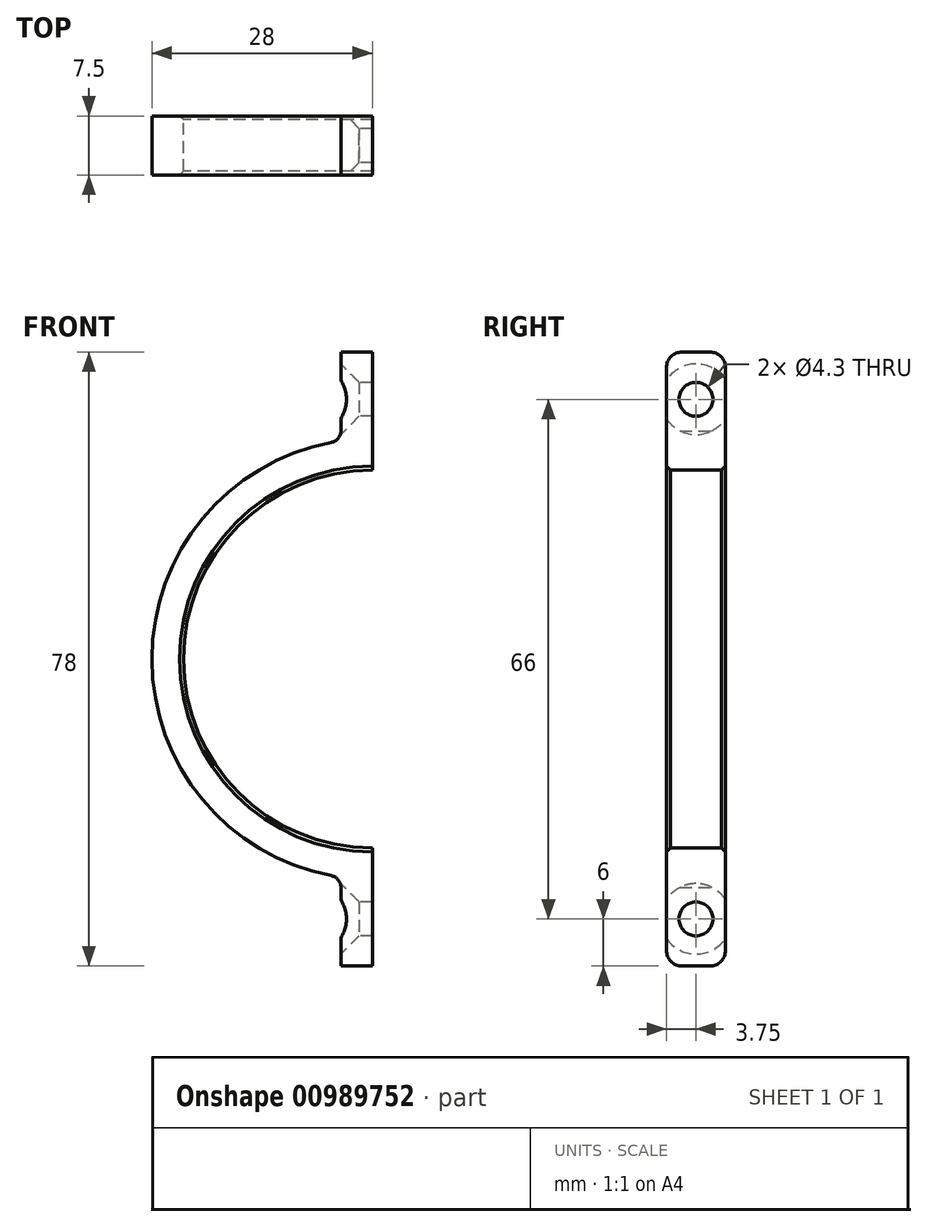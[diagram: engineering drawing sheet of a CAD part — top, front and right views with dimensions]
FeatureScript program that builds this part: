
annotation { "Feature Type Name" : "Feature", "Feature Type Description" : "" }
export const myFeature = defineFeature(function(context is Context, id is Id, definition is map)
    precondition{}
    {
        {
            var Q0;
            Q0=qCreatedBy(makeId("Front.planeOp"),FACE);
            var sketch = newSketch(context, id + "F0", { "sketchPlane" : qUnion([Q0])});
            skArc(sketch, "E0", {"start": v(-5.22, 27.5) * mm, "mid": v(-28, 0) * mm, "end": v(-5.22, -27.5) * mm});
            skArc(sketch, "E1", {"start": v(0, 24) * mm, "mid": v(-24, 0) * mm, "end": v(0, -24) * mm});
            skLineSegment(sketch, "E2", {"start": v(0, 28) * mm, "end": v(0, 24) * mm});
            skLineSegment(sketch, "E3", {"start": v(0, -24) * mm, "end": v(0, -28) * mm});
            skLineSegment(sketch, "E4", {"start": v(-4, 28.98) * mm, "end": v(-4, 39) * mm});
            skLineSegment(sketch, "E5", {"start": v(-4, 39) * mm, "end": v(0, 39) * mm});
            skLineSegment(sketch, "E6", {"start": v(0, 39) * mm, "end": v(0, 28) * mm});
            skLineSegment(sketch, "E7", {"start": v(0, -28) * mm, "end": v(0, -39) * mm});
            skLineSegment(sketch, "E8", {"start": v(0, -39) * mm, "end": v(-4, -39) * mm});
            skLineSegment(sketch, "E9", {"start": v(-4, -39) * mm, "end": v(-4, -28.98) * mm});
            skArc(sketch, "E10", {"start": v(-5.22, 27.5) * mm, "mid": v(-4.34, 28.03) * mm, "end": v(-4, 28.98) * mm});
            skArc(sketch, "E11.MirrorCS", {"start": v(-5.22, -27.5) * mm, "mid": v(-4.34, -28.03) * mm, "end": v(-4, -28.98) * mm});
            skSolve(sketch);
        }
        {
            var Q0;
            Q0=makeQuery(id+"F0.imprint","IMPRINT",FACE,{"disambiguationData":[TD([[makeQuery(id+"F0.imprint","IMPRINT",EDGE,{"derivedFrom":sQuery(id+"F0.wireOp",EDGE,"E0")}),1.0]])]});
            extrude(context, id + "F1", {"entities" : qUnion([Q0]), "depth" : 7.5 * mm, "offsetDistance" : 25 * mm, "symmetric" : true});
        }
        {
            var Q0;
            Q0=makeQuery(id+"F1.opExtrude","SWEPT_FACE",FACE,{"disambiguationData":[OSD([sQuery(id+"F0.wireOp",EDGE,"E9")])]});
            var sketch = newSketch(context, id + "F2", { "sketchPlane" : qUnion([Q0])});
            skPoint(sketch, "E12", {"position": v(0, 33) * mm});
            skPoint(sketch, "E13", {"position": v(0, -33) * mm});
            skSolve(sketch);
        }
        {
            var Q0;
            Q0=sQuery(id+"F2.wireOp",VERTEX,"E12");
            var Q1;
            Q1=sQuery(id+"F2.wireOp",VERTEX,"E13");
            var Q2;
            Q2=makeQuery(id+"F1.opExtrude","SWEPT_BODY",BODY,{"disambiguationData":[OSD([sQuery(id+"F0.wireOp",EDGE,"E0"),sQuery(id+"F0.wireOp",EDGE,"E1"),sQuery(id+"F0.wireOp",EDGE,"E2"),sQuery(id+"F0.wireOp",EDGE,"E3"),sQuery(id+"F0.wireOp",EDGE,"E4"),sQuery(id+"F0.wireOp",EDGE,"E5"),sQuery(id+"F0.wireOp",EDGE,"E6"),sQuery(id+"F0.wireOp",EDGE,"E7"),sQuery(id+"F0.wireOp",EDGE,"E8"),sQuery(id+"F0.wireOp",EDGE,"E9")])]});
            hole(context, id + "F3", {"style" : HoleStyle.C_SINK, "endStyle" : HoleEndStyle.THROUGH, "standardTappedOrClearance" : lookupTablePath({ "fit" : "Close", "standard" : "ISO", "size" : "M4", "type" : "Clearance" }), "standardBlindInLast" : lookupTablePath({ "fit" : "Close", "standard" : "ISO", "engagement" : "75%", "pitch" : "0.7 mm", "size" : "M4", "type" : "Clearance & tapped" }), "holeDiameter" : 4.3 * mm, "cSinkDiameter" : 8.96 * mm, "cSinkAngle" : 90 * degree, "majorDiameter" : 5 * mm, "isTappedThrough" : true, "tappedDepth" : 1 * mm, "tapClearance" : 3, "startFromSketch" : true, "locations" : qUnion([Q0, Q1]), "scope" : qUnion([Q2])});
        }
        {
            var Q0;
            Q0=makeQuery(id+"F1.opExtrude","CAP_EDGE",EDGE,{"disambiguationData":[OSD([sQuery(id+"F0.wireOp",EDGE,"E5")])],"isStart":true});
            var Q1;
            Q1=makeQuery(id+"F1.opExtrude","CAP_EDGE",EDGE,{"disambiguationData":[OSD([sQuery(id+"F0.wireOp",EDGE,"E5")])],"isStart":false});
            var Q2;
            Q2=makeQuery(id+"F1.opExtrude","CAP_EDGE",EDGE,{"disambiguationData":[OSD([sQuery(id+"F0.wireOp",EDGE,"E8")])],"isStart":false});
            var Q3;
            Q3=makeQuery(id+"F1.opExtrude","CAP_EDGE",EDGE,{"disambiguationData":[OSD([sQuery(id+"F0.wireOp",EDGE,"E8")])],"isStart":true});
            fillet(context, id + "F4", {"entities" : qUnion([Q0, Q1, Q2, Q3]), "radius" : 2 * mm, "tangentPropagation" : true, "allowEdgeOverflow" : false});
        }
        {
            var Q0;
            Q0=makeQuery(id+"F1.opExtrude","CAP_EDGE",EDGE,{"disambiguationData":[OSD([sQuery(id+"F0.wireOp",EDGE,"E1")])],"isStart":true});
            var Q1;
            Q1=makeQuery(id+"F1.opExtrude","CAP_EDGE",EDGE,{"disambiguationData":[OSD([sQuery(id+"F0.wireOp",EDGE,"E1")])],"isStart":false});
            chamfer(context, id + "F5", {"entities" : qUnion([Q0, Q1]), "width" : 0.5 * mm, "tangentPropagation" : true});
        }
    });
